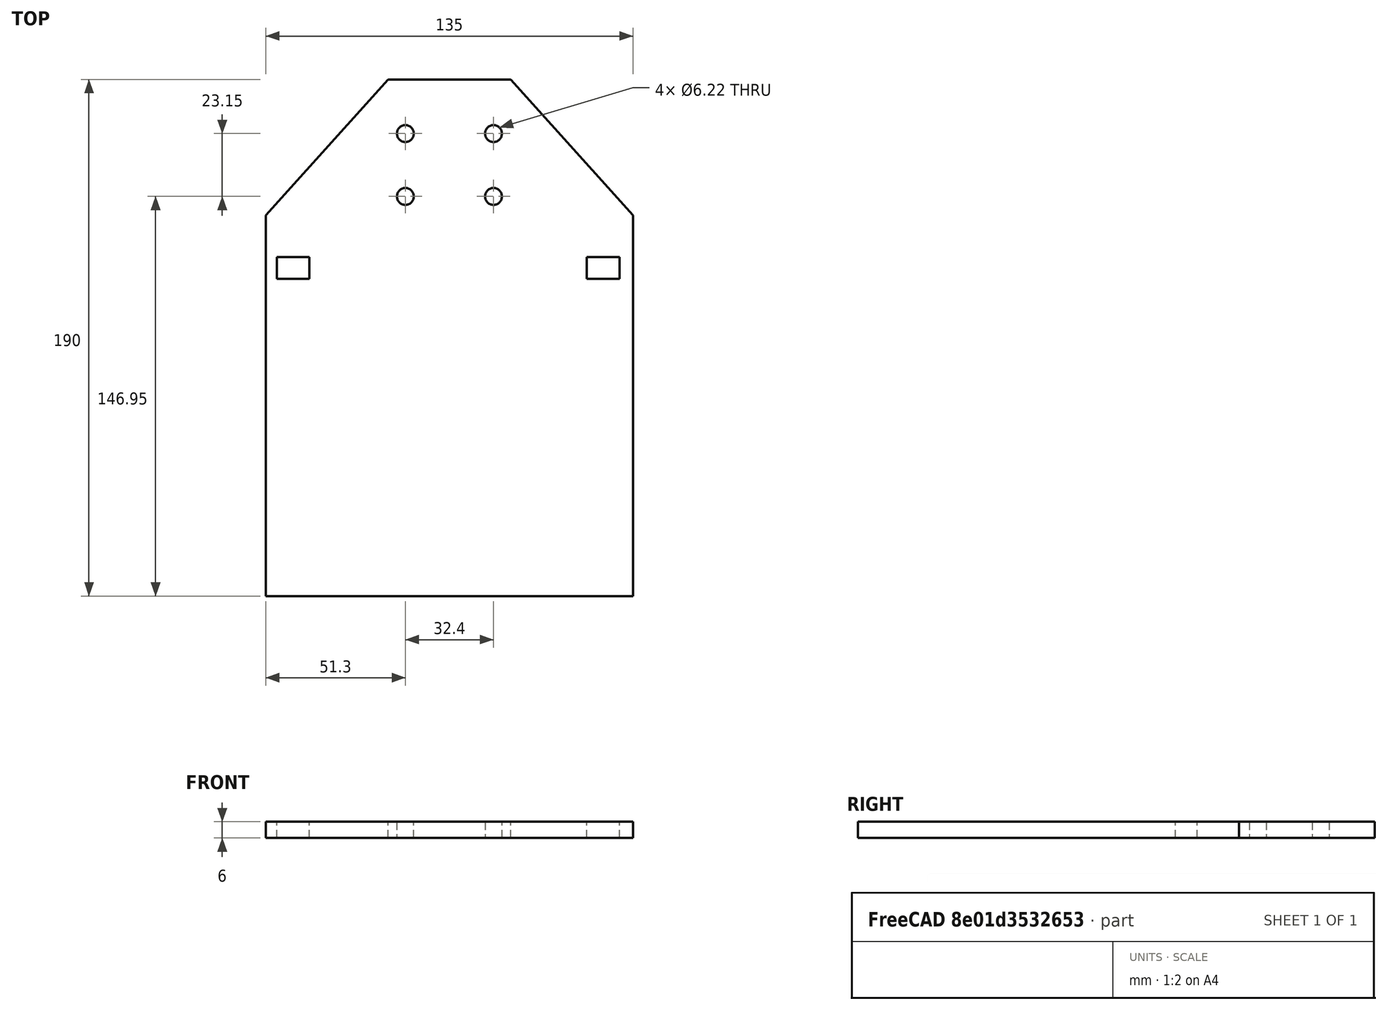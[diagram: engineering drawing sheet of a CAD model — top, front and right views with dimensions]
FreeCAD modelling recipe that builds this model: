
FCSTD DOCUMENT  (FreeCAD 0.20R29410 (Git))
Label: Chassis
License: All rights reserved
LicenseURL: http://en.wikipedia.org/wiki/All_rights_reserved
objects: Sketcher::SketchObject×1, Part::Extrusion×1
note: 2 computed .brp shape members not serialized (recipe doc carries the construction recipe); baked Part::Feature solids carry a one-line shape summary decoded from their .brp

FEATURE [Sketcher::SketchObject] Sketch
  FullyConstrained = true
  sketch-geometry (18):
    g0: LineSegment StartX=0 StartY=0 StartZ=0 EndX=135 EndY=0 EndZ=0
    g1: LineSegment StartX=135 StartY=0 StartZ=0 EndX=135 EndY=140 EndZ=0
    g2: LineSegment StartX=135 StartY=140 StartZ=0 EndX=90 EndY=190 EndZ=0
    g3: LineSegment StartX=90 StartY=190 StartZ=0 EndX=45 EndY=190 EndZ=0
    g4: LineSegment StartX=45 StartY=190 StartZ=0 EndX=0 EndY=140 EndZ=0
    g5: LineSegment StartX=0 StartY=140 StartZ=0 EndX=0 EndY=0 EndZ=0
    g6: Circle CenterX=51.3 CenterY=146.95 CenterZ=0 NormalX=0 NormalY=0 NormalZ=1 AngleXU=0 Radius=3.11
    g7: Circle CenterX=83.7 CenterY=146.95 CenterZ=0 NormalX=0 NormalY=0 NormalZ=1 AngleXU=0 Radius=3.11
    g8: Circle CenterX=51.3 CenterY=170.1 CenterZ=0 NormalX=0 NormalY=0 NormalZ=1 AngleXU=0 Radius=3.11
    g9: Circle CenterX=83.7 CenterY=170.1 CenterZ=0 NormalX=0 NormalY=0 NormalZ=1 AngleXU=0 Radius=3.11
    g10: LineSegment StartX=118 StartY=124.7 StartZ=0 EndX=130 EndY=124.7 EndZ=0
    g11: LineSegment StartX=130 StartY=124.7 StartZ=0 EndX=130 EndY=116.7 EndZ=0
    g12: LineSegment StartX=130 StartY=116.7 StartZ=0 EndX=118 EndY=116.7 EndZ=0
    g13: LineSegment StartX=118 StartY=116.7 StartZ=0 EndX=118 EndY=124.7 EndZ=0
    g14: LineSegment StartX=4 StartY=124.7 StartZ=0 EndX=16 EndY=124.7 EndZ=0
    g15: LineSegment StartX=16 StartY=124.7 StartZ=0 EndX=16 EndY=116.7 EndZ=0
    g16: LineSegment StartX=16 StartY=116.7 StartZ=0 EndX=4 EndY=116.7 EndZ=0
    g17: LineSegment StartX=4 StartY=116.7 StartZ=0 EndX=4 EndY=124.7 EndZ=0
  constraints (53):
    c: Coincident(g0,g-1)
    c: PointOnObject(g0,g-1)
    c: Coincident(g1,g0)
    c: Vertical(g1)
    c: Horizontal(g3)
    c: Coincident(g4,g3)
    c: PointOnObject(g4,g-2)
    c: Coincident(g5,g0)
    c: Coincident(g2,g3)
    c: Coincident(g4,g5)
    c: Coincident(g1,g2)
    c: Equal(g5,g1)
    c: DistanceX(g0,g0) = 135
    c: DistanceY(g1,g1) = 140
    c: Equal(g4,g2)
    c: DistanceY(g2,g2) = 50
    c: DistanceX(g2,g2) = 45
    c: Equal(g6,g8)
    c: Equal(g8,g9)
    c: Equal(g9,g7)
    c: Horizontal(g6,g7)
    c: Horizontal(g8,g9)
    c: Vertical(g6,g8)
    c: Vertical(g9,g7)
    c: DistanceX(g7,g1) = 51.3
    c: DistanceX(g4,g6) = 51.3
    c: DistanceY(g9,g2) = 19.9
    c: DistanceY(g6,g8) = 23.15
    c: Radius(g8) = 3.11
    c: Coincident(g10,g11)
    c: Coincident(g11,g12)
    c: Coincident(g12,g13)
    c: Coincident(g13,g10)
    c: Horizontal(g10)
    c: Horizontal(g12)
    c: Vertical(g11)
    c: Vertical(g13)
    c: Coincident(g14,g15)
    c: Coincident(g15,g16)
    c: Coincident(g16,g17)
    c: Coincident(g17,g14)
    c: Horizontal(g14)
    c: Horizontal(g16)
    c: Vertical(g15)
    c: Vertical(g17)
    c: DistanceX(g4,g14) = 4
    c: DistanceX(g10,g1) = 5
    c: DistanceX(g14,g14) = 12
    c: DistanceY(g15,g15) = 8
    c: Equal(g14,g10)
    c: Equal(g15,g13)
    c: Horizontal(g14,g10)
    c: DistanceY(g10,g1) = 15.3
FEATURE [Part::Extrusion] Extrude
  Base = -> Sketch
  Dir = (0,0,1)
  DirMode = 2
  FaceMakerClass = Part::FaceMakerBullseye
  LengthFwd = 6
  LengthRev = 0
  Solid = true
  Symmetric = false
